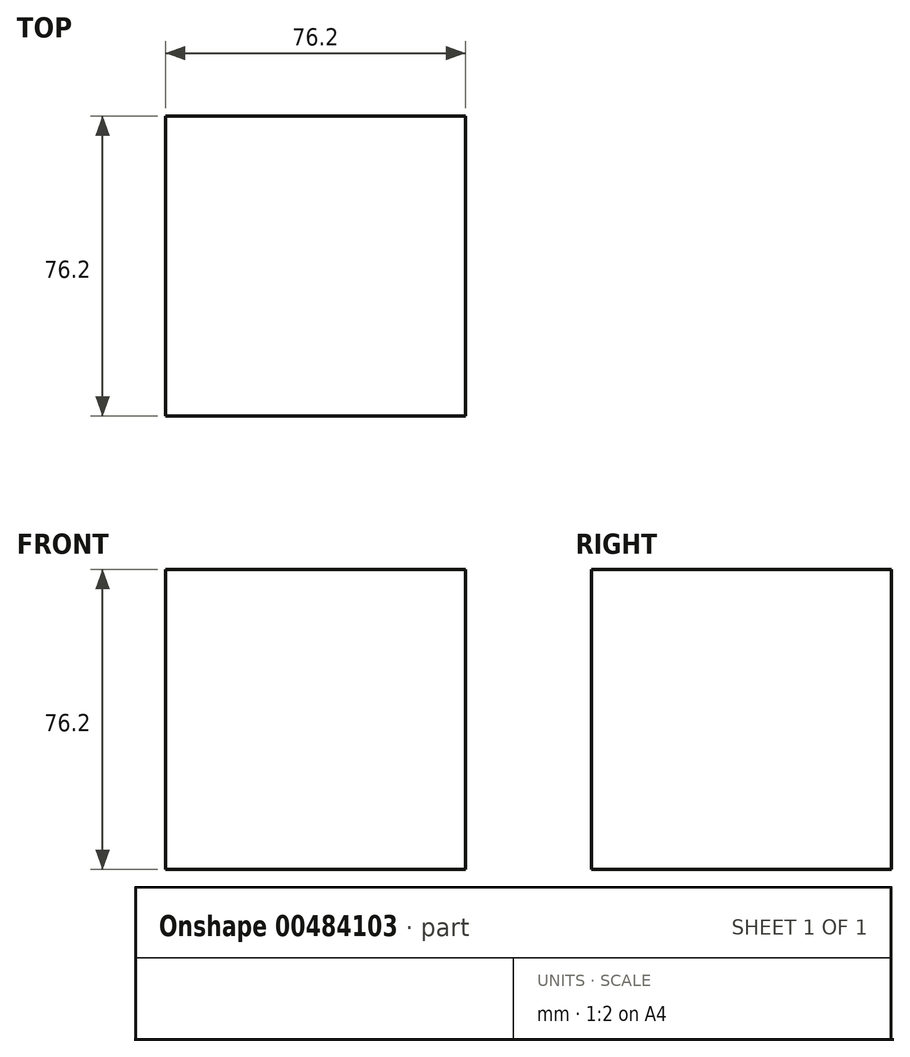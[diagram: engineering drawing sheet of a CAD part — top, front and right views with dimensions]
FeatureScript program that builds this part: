
annotation { "Feature Type Name" : "Feature", "Feature Type Description" : "" }
export const myFeature = defineFeature(function(context is Context, id is Id, definition is map)
    precondition{}
    {
        {
            var Q0;
            Q0=qCreatedBy(makeId("Right.planeOp"),FACE);
            var sketch = newSketch(context, id + "F0", { "sketchPlane" : qUnion([Q0])});
            skLineSegment(sketch, "E0.bottom", {"start": v(38.1, -38.1) * mm, "end": v(-38.1, -38.1) * mm});
            skLineSegment(sketch, "E0.top", {"start": v(38.1, 38.1) * mm, "end": v(-38.1, 38.1) * mm});
            skLineSegment(sketch, "E0.left", {"start": v(38.1, -38.1) * mm, "end": v(38.1, 38.1) * mm});
            skLineSegment(sketch, "E0.right", {"start": v(-38.1, -38.1) * mm, "end": v(-38.1, 38.1) * mm});
            skPoint(sketch, "E0.middle", {"position": v(0, 0) * mm});
            skSolve(sketch);
        }
        {
            var Q0;
            Q0 = qSketchRegion(id + "F0", true);
            extrude(context, id + "F1", {"entities" : qUnion([Q0]), "endBound" : BoundingType.SYMMETRIC, "depth" : 76.2 * mm});
        }
    });
